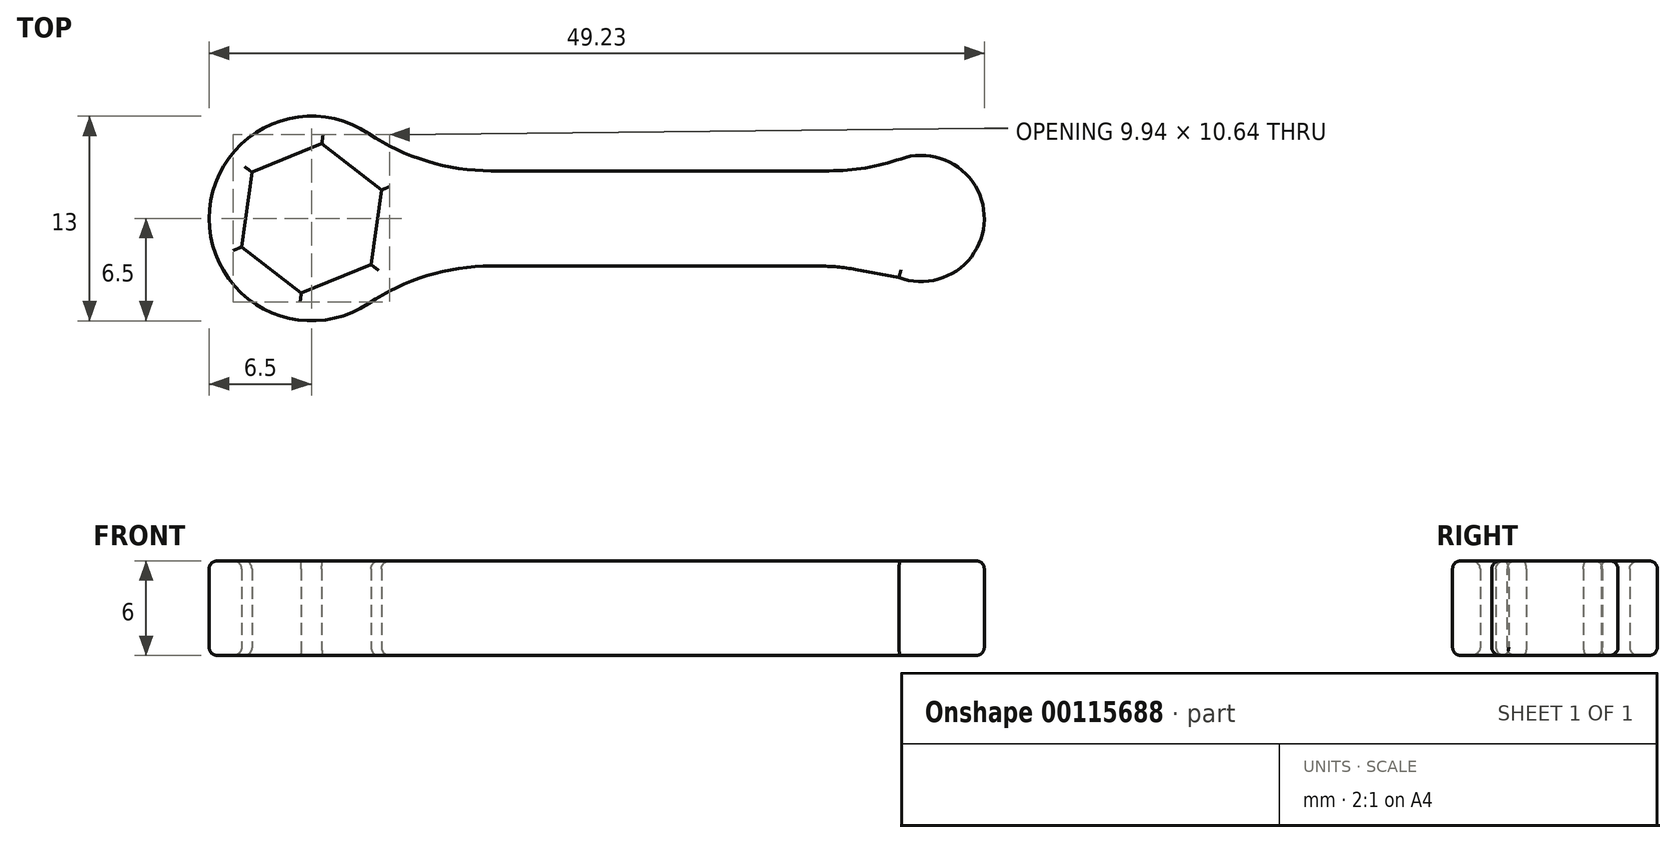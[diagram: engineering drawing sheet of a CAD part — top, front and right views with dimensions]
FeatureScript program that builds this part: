
annotation { "Feature Type Name" : "Feature", "Feature Type Description" : "" }
export const myFeature = defineFeature(function(context is Context, id is Id, definition is map)
    precondition{}
    {
        {
            var Q0;
            Q0=qCreatedBy(makeId("Top.planeOp"),FACE);
            var sketch = newSketch(context, id + "F0", { "sketchPlane" : qUnion([Q0])});
            skCircle(sketch, "E0.cCircle", {"center": v(0, 0) * mm, "radius": 4.15 * mm, "construction": true});
            skLineSegment(sketch, "E0.0", {"start": v(0.65, 4.75) * mm, "end": v(4.44, 1.81) * mm});
            skLineSegment(sketch, "E0.1", {"start": v(4.44, 1.81) * mm, "end": v(3.79, -2.94) * mm});
            skLineSegment(sketch, "E0.2", {"start": v(3.79, -2.94) * mm, "end": v(-0.65, -4.75) * mm});
            skLineSegment(sketch, "E0.3", {"start": v(-0.65, -4.75) * mm, "end": v(-4.44, -1.81) * mm});
            skLineSegment(sketch, "E0.4", {"start": v(-4.44, -1.81) * mm, "end": v(-3.79, 2.94) * mm});
            skLineSegment(sketch, "E0.5", {"start": v(-3.79, 2.94) * mm, "end": v(0.65, 4.75) * mm});
            skPoint(sketch, "E0.0.midPoint", {"position": v(2.54, 3.28) * mm});
            skArc(sketch, "E1", {"start": v(5.75, 3.03) * mm, "mid": v(-6.5, 0) * mm, "end": v(5.75, -3.03) * mm});
            skLineSegment(sketch, "E2", {"start": v(21.8, 9.69) * mm, "end": v(21.8, -18.05) * mm, "construction": true});
            skLineSegment(sketch, "E3", {"start": v(0, 0) * mm, "end": v(49.97, 0) * mm, "construction": true});
            skLineSegment(sketch, "E4", {"start": v(5.75, 3.03) * mm, "end": v(36.1, 3.03) * mm});
            skLineSegment(sketch, "E5.MirrorCS", {"start": v(5.75, -3.03) * mm, "end": v(36.1, -3.03) * mm});
            skArc(sketch, "E6", {"start": v(36.1, -3.03) * mm, "mid": v(42.73, 0) * mm, "end": v(36.1, 3.03) * mm});
            skSolve(sketch);
        }
        {
            var Q0;
            Q0=qSketchRegion(id+"F0",true);
            extrude(context, id + "F1", {"entities" : qUnion([Q0]), "depth" : 6 * mm});
        }
        {
            var Q0;
            Q0=makeQuery(id+"F1.opExtrude","SWEPT_EDGE",EDGE,{"disambiguationData":[OSD([sQuery(id+"F0.wireOp",EDGE,"E4"),sQuery(id+"F0.wireOp",EDGE,"43233ae7-7179-43de-99ca-32c86b7c7e03.trimOffspring")])]});
            var Q1;
            Q1=makeQuery(id+"F1.opExtrude","SWEPT_EDGE",EDGE,{"disambiguationData":[OSD([sQuery(id+"F0.wireOp",EDGE,"E1"),sQuery(id+"F0.wireOp",EDGE,"E5.MirrorCS")])]});
            var Q2;
            Q2=makeQuery(id+"F1.opExtrude","SWEPT_EDGE",EDGE,{"disambiguationData":[OSD([sQuery(id+"F0.wireOp",EDGE,"E1"),sQuery(id+"F0.wireOp",EDGE,"E4")])]});
            fillet(context, id + "F2", {"entities" : qUnion([Q0, Q1, Q2]), "radius" : 14 * mm, "tangentPropagation" : true, "allowEdgeOverflow" : false});
        }
        {
            var Q0;
            Q0=makeQuery(id+"F1.opExtrude","SWEPT_EDGE",EDGE,{"disambiguationData":[OSD([sQuery(id+"F0.wireOp",EDGE,"4d8174f4-63f9-4eef-a5dd-54be3253088e3.MirrorC"),sQuery(id+"F0.wireOp",EDGE,"E5.MirrorCS")])]});
            chamfer(context, id + "F3", {"entities" : qUnion([Q0]), "width" : 11 * mm, "tangentPropagation" : true});
        }
        {
            var Q0;
            {var subQ0=sQuery(id+"F0.wireOp",EDGE,"4d8174f4-63f9-4eef-a5dd-54be3253088e3.MirrorC");Q0=makeQuery(id+"F3.opChamfer","BLEND_EDGE",EDGE,{"blendedFrom":[makeQuery(id+"F1.opExtrude","SWEPT_EDGE",EDGE,{"disambiguationData":[OSD([subQ0,sQuery(id+"F0.wireOp",EDGE,"E5.MirrorCS")])]}),makeQuery(id+"F1.opExtrude","SWEPT_FACE",FACE,{"disambiguationData":[OSD([subQ0])]})],"blendedInto":[makeQuery(id+"F1.opExtrude","SWEPT_FACE",FACE,{"disambiguationData":[OSD([subQ0])]})]});}
            var Q1;
            {var subQ0=sQuery(id+"F0.wireOp",EDGE,"E5.MirrorCS");Q1=makeQuery(id+"F3.opChamfer","BLEND_EDGE",EDGE,{"blendedFrom":[makeQuery(id+"F1.opExtrude","SWEPT_EDGE",EDGE,{"disambiguationData":[OSD([sQuery(id+"F0.wireOp",EDGE,"4d8174f4-63f9-4eef-a5dd-54be3253088e3.MirrorC"),subQ0])]}),makeQuery(id+"F1.opExtrude","SWEPT_FACE",FACE,{"disambiguationData":[OSD([subQ0])]})],"blendedInto":[makeQuery(id+"F1.opExtrude","SWEPT_FACE",FACE,{"disambiguationData":[OSD([subQ0])]})]});}
            fillet(context, id + "F4", {"entities" : qUnion([Q0, Q1]), "radius" : 13 * mm, "tangentPropagation" : true, "allowEdgeOverflow" : false});
        }
        {
            var Q0;
            Q0=makeQuery(id+"F1.opExtrude","CAP_FACE",FACE,{"disambiguationData":[OSD([sQuery(id+"F0.wireOp",EDGE,"E0.0"),sQuery(id+"F0.wireOp",EDGE,"E0.1"),sQuery(id+"F0.wireOp",EDGE,"E0.2"),sQuery(id+"F0.wireOp",EDGE,"E0.3"),sQuery(id+"F0.wireOp",EDGE,"E0.4"),sQuery(id+"F0.wireOp",EDGE,"E0.5"),sQuery(id+"F0.wireOp",EDGE,"E1"),sQuery(id+"F0.wireOp",EDGE,"4d8174f4-63f9-4eef-a5dd-54be3253088e0.MirrorCS"),sQuery(id+"F0.wireOp",EDGE,"4d8174f4-63f9-4eef-a5dd-54be3253088e1.MirrorCS"),sQuery(id+"F0.wireOp",EDGE,"4d8174f4-63f9-4eef-a5dd-54be3253088e2.MirrorCS"),sQuery(id+"F0.wireOp",EDGE,"4d8174f4-63f9-4eef-a5dd-54be3253088e3.MirrorC"),sQuery(id+"F0.wireOp",EDGE,"4d8174f4-63f9-4eef-a5dd-54be3253088e7.MirrorCS"),sQuery(id+"F0.wireOp",EDGE,"E4"),sQuery(id+"F0.wireOp",EDGE,"E5.MirrorCS"),sQuery(id+"F0.wireOp",EDGE,"ANH0onW4-scqo-v5nj-Zf9w-YCJY64Ime78A"),sQuery(id+"F0.wireOp",EDGE,"aAK1G2DO-I9rq-uXcD-boOl-0NSTUN64LIbU"),sQuery(id+"F0.wireOp",EDGE,"43233ae7-7179-43de-99ca-32c86b7c7e03.trimOffspring")])],"isStart":true});
            var Q1;
            Q1=makeQuery(id+"F1.opExtrude","CAP_FACE",FACE,{"disambiguationData":[OSD([sQuery(id+"F0.wireOp",EDGE,"E0.0"),sQuery(id+"F0.wireOp",EDGE,"E0.1"),sQuery(id+"F0.wireOp",EDGE,"E0.2"),sQuery(id+"F0.wireOp",EDGE,"E0.3"),sQuery(id+"F0.wireOp",EDGE,"E0.4"),sQuery(id+"F0.wireOp",EDGE,"E0.5"),sQuery(id+"F0.wireOp",EDGE,"E1"),sQuery(id+"F0.wireOp",EDGE,"4d8174f4-63f9-4eef-a5dd-54be3253088e0.MirrorCS"),sQuery(id+"F0.wireOp",EDGE,"4d8174f4-63f9-4eef-a5dd-54be3253088e1.MirrorCS"),sQuery(id+"F0.wireOp",EDGE,"4d8174f4-63f9-4eef-a5dd-54be3253088e2.MirrorCS"),sQuery(id+"F0.wireOp",EDGE,"4d8174f4-63f9-4eef-a5dd-54be3253088e3.MirrorC"),sQuery(id+"F0.wireOp",EDGE,"4d8174f4-63f9-4eef-a5dd-54be3253088e7.MirrorCS"),sQuery(id+"F0.wireOp",EDGE,"E4"),sQuery(id+"F0.wireOp",EDGE,"E5.MirrorCS"),sQuery(id+"F0.wireOp",EDGE,"ANH0onW4-scqo-v5nj-Zf9w-YCJY64Ime78A"),sQuery(id+"F0.wireOp",EDGE,"aAK1G2DO-I9rq-uXcD-boOl-0NSTUN64LIbU"),sQuery(id+"F0.wireOp",EDGE,"43233ae7-7179-43de-99ca-32c86b7c7e03.trimOffspring")])],"isStart":false});
            fillet(context, id + "F5", {"entities" : qUnion([Q0, Q1]), "radius" : 0.5 * mm, "tangentPropagation" : true, "allowEdgeOverflow" : false});
        }
    });
